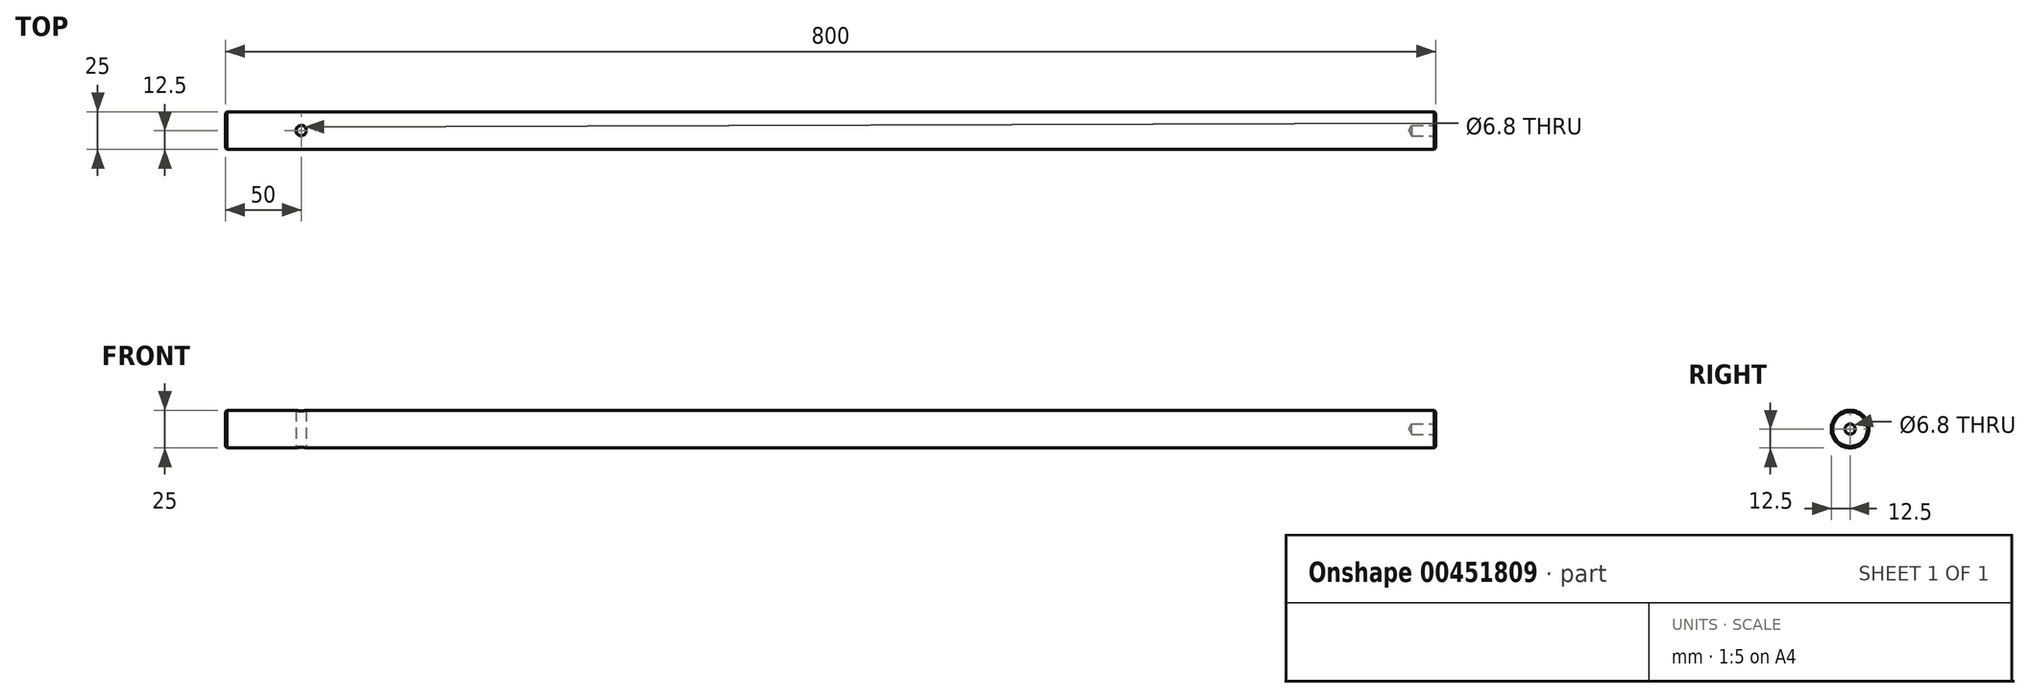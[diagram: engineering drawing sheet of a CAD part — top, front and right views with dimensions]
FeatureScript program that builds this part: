
annotation { "Feature Type Name" : "Feature", "Feature Type Description" : "" }
export const myFeature = defineFeature(function(context is Context, id is Id, definition is map)
    precondition{}
    {
        {
            var Q0;
            Q0=qCreatedBy(makeId("Right.planeOp"),FACE);
            var sketch = newSketch(context, id + "F0", { "sketchPlane" : qUnion([Q0])});
            skCircle(sketch, "E0", {"center": v(0, 0) * mm, "radius": 12.5 * mm});
            skSolve(sketch);
        }
        {
            var Q0;
            Q0 = qSketchRegion(id + "F0", true);
            extrude(context, id + "F1", {"entities" : qUnion([Q0]), "endBound" : BoundingType.SYMMETRIC, "depth" : 800 * mm});
        }
        {
            var Q0;
            Q0=makeQuery(id+"F1.opExtrude","CAP_FACE",FACE,{"disambiguationData":[OSD([sQuery(id+"F0.wireOp",EDGE,"E0")])],"isStart":false});
            var sketch = newSketch(context, id + "F2", { "sketchPlane" : qUnion([Q0])});
            skPoint(sketch, "E1", {"position": v(0, 0) * mm});
            skSolve(sketch);
        }
        {
            var Q0;
            Q0=sQuery(id+"F2.wireOp",VERTEX,"E1");
            var Q1;
            Q1=makeQuery(id+"F1.opExtrude","SWEPT_BODY",BODY,{"disambiguationData":[OSD([sQuery(id+"F0.wireOp",EDGE,"E0")])]});
            hole(context, id + "F3", {"style" : HoleStyle.SIMPLE, "endStyle" : HoleEndStyle.BLIND, "standardTappedOrClearance" : lookupTablePath({ "standard" : "ISO", "engagement" : "75%", "pitch" : "1.25 mm", "size" : "M8", "type" : "Tapped" }), "standardBlindInLast" : lookupTablePath({ "standard" : "ISO", "engagement" : "75%", "pitch" : "1.25 mm", "size" : "M8", "type" : "Tapped" }), "holeDiameter" : 6.8 * mm, "showTappedDepth" : true, "holeDepth" : 15.75 * mm, "isTappedThrough" : true, "tappedDepth" : 12 * mm, "tapClearance" : 3, "locations" : qUnion([Q0]), "scope" : qUnion([Q1]), "majorDiameter" : 8 * mm});
        }
        {
            var Q0;
            Q0=makeQuery(id+"F1.opExtrude","CAP_EDGE",EDGE,{"disambiguationData":[OSD([sQuery(id+"F0.wireOp",EDGE,"E0")])],"isStart":false});
            var Q1;
            Q1=makeQuery(id+"F1.opExtrude","CAP_EDGE",EDGE,{"disambiguationData":[OSD([sQuery(id+"F0.wireOp",EDGE,"E0")])],"isStart":true});
            chamfer(context, id + "F4", {"entities" : qUnion([Q0, Q1]), "width" : 1 * mm, "tangentPropagation" : true});
        }
        {
            var Q0;
            Q0=qCreatedBy(makeId("Top.planeOp"),FACE);
            var sketch = newSketch(context, id + "F5", { "sketchPlane" : qUnion([Q0])});
            skPoint(sketch, "E2", {"position": v(-350, 0) * mm});
            skSolve(sketch);
        }
        {
            var Q0;
            Q0=sQuery(id+"F5.wireOp",VERTEX,"E2");
            var Q1;
            Q1=makeQuery(id+"F1.opExtrude","SWEPT_BODY",BODY,{"disambiguationData":[OSD([sQuery(id+"F0.wireOp",EDGE,"E0")])]});
            hole(context, id + "F6", {"style" : HoleStyle.SIMPLE, "endStyle" : HoleEndStyle.THROUGH, "oppositeDirection" : true, "standardTappedOrClearance" : lookupTablePath({ "standard" : "ISO", "engagement" : "75%", "pitch" : "1.25 mm", "size" : "M8", "type" : "Tapped" }), "standardBlindInLast" : lookupTablePath({ "standard" : "ISO", "engagement" : "75%", "pitch" : "1.25 mm", "size" : "M8", "type" : "Tapped" }), "holeDiameter" : 6.8 * mm, "showTappedDepth" : true, "isTappedThrough" : true, "tappedDepth" : 12 * mm, "tapClearance" : 3, "locations" : qUnion([Q0]), "scope" : qUnion([Q1]), "majorDiameter" : 8 * mm});
        }
        {
            var Q0;
            Q0=sQuery(id+"F5.wireOp",VERTEX,"E2");
            var Q1;
            Q1=makeQuery(id+"F1.opExtrude","SWEPT_BODY",BODY,{"disambiguationData":[OSD([sQuery(id+"F0.wireOp",EDGE,"E0")])]});
            hole(context, id + "F7", {"style" : HoleStyle.SIMPLE, "endStyle" : HoleEndStyle.THROUGH, "standardTappedOrClearance" : lookupTablePath({ "standard" : "ISO", "engagement" : "75%", "pitch" : "1.25 mm", "size" : "M8", "type" : "Tapped" }), "standardBlindInLast" : lookupTablePath({ "standard" : "ISO", "engagement" : "75%", "pitch" : "1.25 mm", "size" : "M8", "type" : "Tapped" }), "holeDiameter" : 6.8 * mm, "showTappedDepth" : true, "isTappedThrough" : true, "tappedDepth" : 12 * mm, "tapClearance" : 3, "locations" : qUnion([Q0]), "scope" : qUnion([Q1]), "majorDiameter" : 8 * mm});
        }
    });
